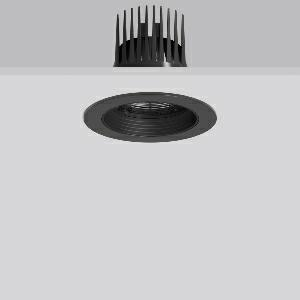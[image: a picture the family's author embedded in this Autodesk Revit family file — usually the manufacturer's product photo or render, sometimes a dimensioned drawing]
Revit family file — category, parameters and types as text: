
# Revit family: heledon_maxi_e_901762_003_1_76_0b55
name_source: partatom
category: Lighting Fixtures
units: mm (PartAtom-declared; Revit-internal decimal feet)

## family parameters
Cut with Voids When Loaded = No
Host = Face
Light Source = No
Part Type = Normal
Room Calculation Point = No
Round Connector Dimension = Use Diameter
Shared = No

## types (1)
- HELEDON maxi E (1 x LED Modul 940, 2950 lm, 4000)
    Apparent Load = 25 VA
    Approval mark = CE
    CIE Flux Codes = 96 100 100 100 100
    Color Rendering = 92
    Color Temperature = 4000
    Default Elevation = 1800 mm
    Description = Series: HELEDON maxi
Round recessed downlight. Housing: die-cast aluminium, powder-coated. Black plastic ring and recessed LED to prevent glare from the side. Optical assembly with lens made of plastic (polycarbonate) for the best homogeneous light distribution - can be changed without tools. Best colour rendering index Ra>90. Suitable for Recessed ceiling mounting. Installation without tools thanks to spring fastening system. Including separate LED converter with connecting cable 600 mm.High quality converter without flickering and stroboscopic effect. Through-wiring box (5 pole) available as accessory. The following accessories can be mounted without use of tools: interchangeable lenses, decorative glasses, honeycomb louvre, clear and frosted diffusers, white interchangeable plastic ring. 
Colour: deep black, matt (RAL 9005)
Diameter: 162 mm
Height: 3 mm
Cut-out diameter: 152 mm
Recess height: 200 mm
Luminaire: recess height: 135 mm
Lamp: LED
Socket: without socket
Colour temperature: 4000K
Colour rendering index (CRI): 92
System power: 25 W
Rated luminous flux: 2950 lm
Luminous efficiency: 118 lm/W
Control gear: Converter, dimmable, DALI
Protection class: II
Type of protection: IP 20
    Height = 0 mm  [stored 0 ft]
    Lamp = 1 x LED Modul 940
    Lamp Light Flux = 2950 lm
    Lamp count = 1
    Length = 162 mm
    Lifetime = 50000 h
    Luminous efficacy = 118 lm/W
    Manufacturer = RZB
    ModVariant = No
    Model = 901762.003.1.76
    Mounting Place = Ceiling
    Mounting Type = Recessed
    Number of Poles = 1
    OnlyDefault = Yes
    Power Factor = 1
    Product Name = HELEDON maxi E
    Product group = Recessed downlights
    ProductGroupID = 402
    Protection Class = Protection class II
    Protection Degree = IP 20
    RLX_Detail_Level = 1
    RLX_Emergency_Light_Flux = 0 lm
    RLX_Emergency_Type = 0
    RLX_Emergency_Type_DB = No
    RlxData = <blob elided: 119333 chars, md5=5210f200>
    Socket = socket
    Standby Power = 0 W
    System Light Flux = 2950 lm
    System Power = 25 W
    Type Comments = Product without accessories
    Type Image = 901663.003.jpg
    URL = http://relux.com
    VarID = ---
    Voltage = 230 V
    Voltage Range = 220-240 V
    Weight = 0.00 kg
    Width = 0 mm  [stored 0 ft]

note: [stored X ft] marks values corroborated as IEEE doubles in the binary element streams (Revit-internal decimal feet)

## geometry (parser evidence)
native form markers: Blend x4, Sweep x11
no freeform markers — native parametric forms only
